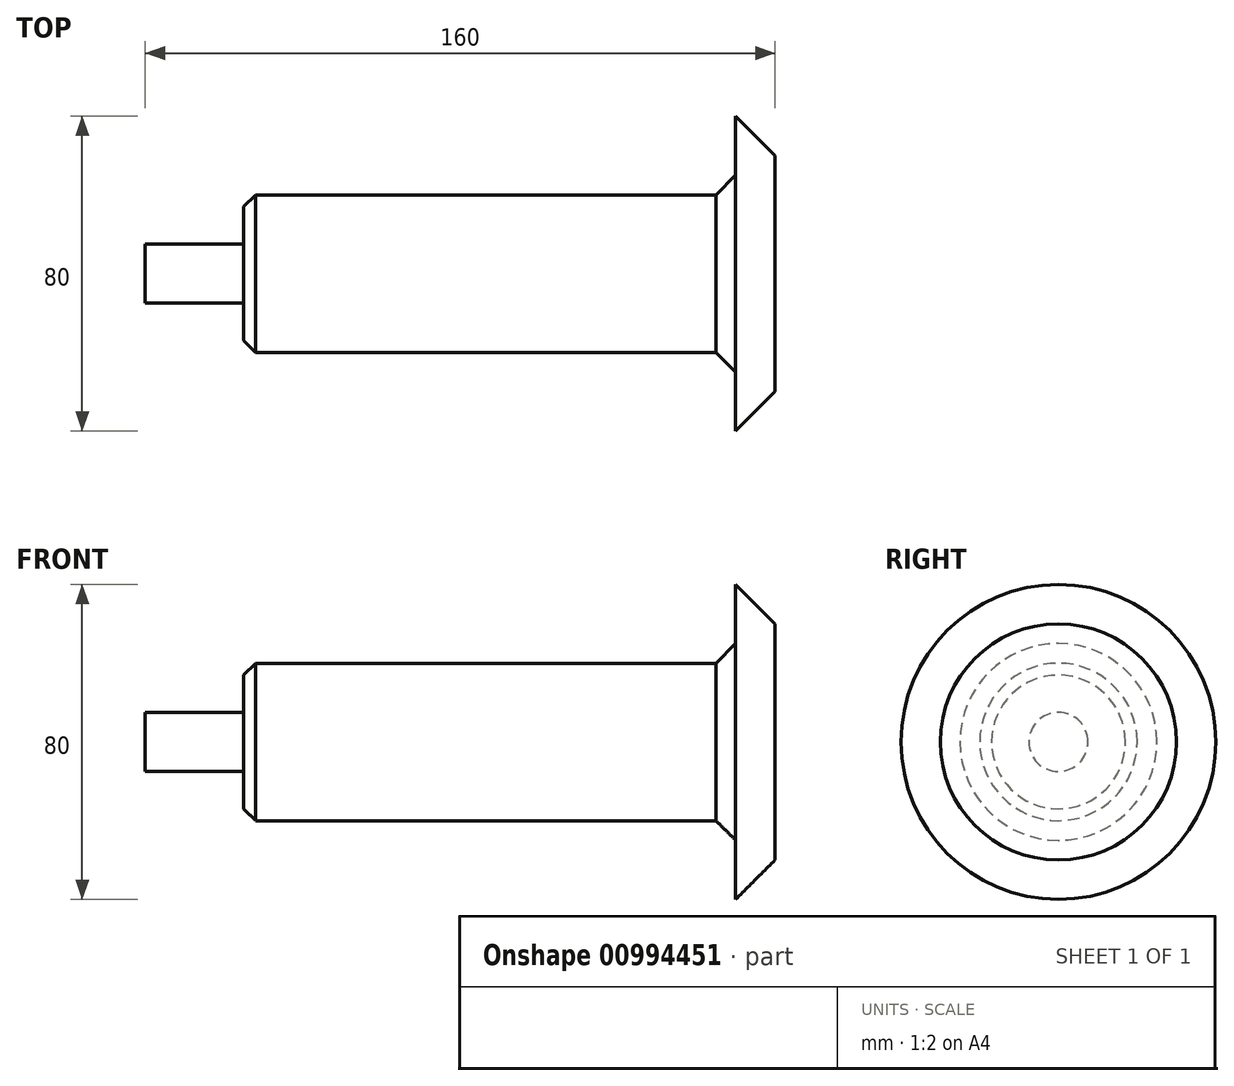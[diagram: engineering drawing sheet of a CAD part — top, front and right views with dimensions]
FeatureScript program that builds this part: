
annotation { "Feature Type Name" : "Feature", "Feature Type Description" : "" }
export const myFeature = defineFeature(function(context is Context, id is Id, definition is map)
    precondition{}
    {
        {
            var Q0;
            Q0=qCreatedBy(makeId("Right.planeOp"),FACE);
            var sketch = newSketch(context, id + "F0", { "sketchPlane" : qUnion([Q0])});
            skCircle(sketch, "E0", {"center": v(0, 0) * mm, "radius": 40 * mm});
            skCircle(sketch, "E1", {"center": v(0, 0) * mm, "radius": 25 * mm});
            skCircle(sketch, "E2", {"center": v(0, 0) * mm, "radius": 20 * mm});
            skCircle(sketch, "E3", {"center": v(0, 0) * mm, "radius": 7.5 * mm});
            skSolve(sketch);
        }
        {
            var Q0;
            Q0=makeQuery(id+"F0.imprint","IMPRINT",FACE,{"disambiguationData":[TD([[makeQuery(id+"F0.imprint","IMPRINT",EDGE,{"derivedFrom":sQuery(id+"F0.wireOp",EDGE,"E0")}),1.0]])]});
            extrude(context, id + "F1", {"entities" : qUnion([Q0]), "oppositeDirection" : true, "depth" : 10 * mm, "offsetDistance" : 25 * mm});
        }
        {
            var Q0;
            Q0=makeQuery(id+"F0.imprint","IMPRINT",FACE,{"disambiguationData":[TD([[makeQuery(id+"F0.imprint","IMPRINT",EDGE,{"derivedFrom":sQuery(id+"F0.wireOp",EDGE,"E1")}),1.0]])]});
            extrude(context, id + "F2", {"entities" : qUnion([Q0]), "operationType" : NewBodyOperationType.ADD, "oppositeDirection" : true, "depth" : 20 * mm, "offsetDistance" : 25 * mm});
        }
        {
            var Q0;
            Q0=makeQuery(id+"F0.imprint","IMPRINT",FACE,{"disambiguationData":[TD([[makeQuery(id+"F0.imprint","IMPRINT",EDGE,{"derivedFrom":sQuery(id+"F0.wireOp",EDGE,"E2")}),1.0]])]});
            extrude(context, id + "F3", {"entities" : qUnion([Q0]), "operationType" : NewBodyOperationType.ADD, "oppositeDirection" : true, "depth" : 135 * mm, "offsetDistance" : 25 * mm});
        }
        {
            var Q0;
            Q0=makeQuery(id+"F0.imprint","IMPRINT",FACE,{"disambiguationData":[TD([[makeQuery(id+"F0.imprint","IMPRINT",EDGE,{"derivedFrom":sQuery(id+"F0.wireOp",EDGE,"E3")}),1.0]])]});
            extrude(context, id + "F4", {"entities" : qUnion([Q0]), "operationType" : NewBodyOperationType.ADD, "oppositeDirection" : true, "depth" : 160 * mm, "offsetDistance" : 25 * mm});
        }
        {
            var Q0;
            Q0=makeQuery(id+"F1.opExtrude","CAP_EDGE",EDGE,{"disambiguationData":[OSD([sQuery(id+"F0.wireOp",EDGE,"E0")])],"isStart":true});
            var Q1;
            Q1=makeQuery(id+"F2.opExtrude","CAP_EDGE",EDGE,{"disambiguationData":[OSD([sQuery(id+"F0.wireOp",EDGE,"E1")])],"isStart":false});
            chamfer(context, id + "F5", {"entities" : qUnion([Q0, Q1]), "chamferType" : ChamferType.OFFSET_ANGLE, "width" : 10 * mm, "oppositeDirection" : false, "angle" : 45 * degree, "tangentPropagation" : true});
        }
        {
            var Q0;
            Q0=makeQuery(id+"F3.opExtrude","CAP_EDGE",EDGE,{"disambiguationData":[OSD([sQuery(id+"F0.wireOp",EDGE,"E2")])],"isStart":false});
            chamfer(context, id + "F6", {"entities" : qUnion([Q0]), "chamferType" : ChamferType.OFFSET_ANGLE, "width" : 3 * mm, "oppositeDirection" : false, "angle" : 45 * degree, "tangentPropagation" : true});
        }
    });
